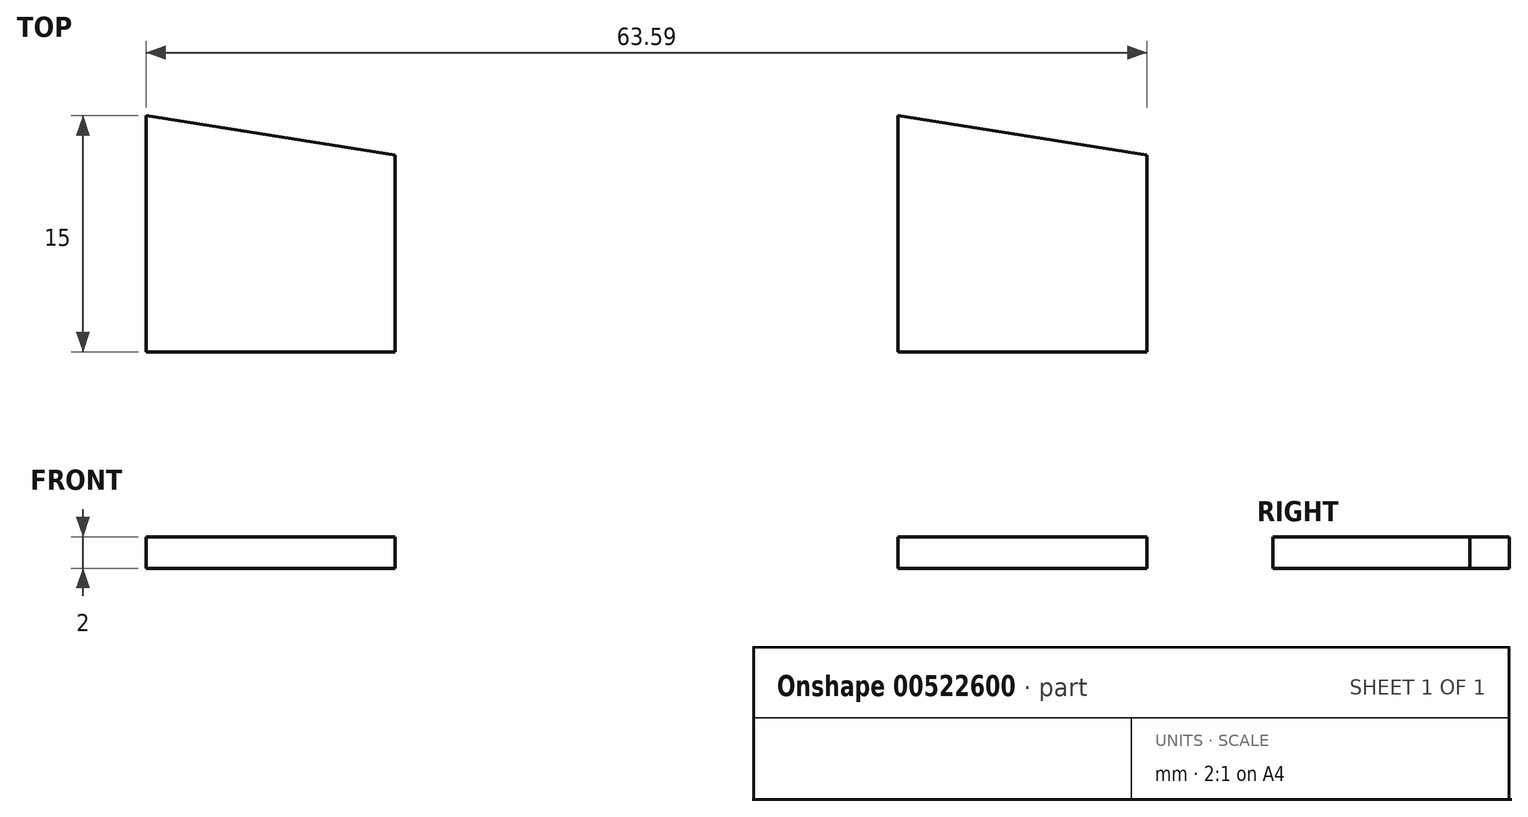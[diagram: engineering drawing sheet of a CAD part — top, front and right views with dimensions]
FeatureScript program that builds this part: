
annotation { "Feature Type Name" : "Feature", "Feature Type Description" : "" }
export const myFeature = defineFeature(function(context is Context, id is Id, definition is map)
    precondition{}
    {
        {
            var Q0;
            Q0=qCreatedBy(makeId("Top.planeOp"),FACE);
            var sketch = newSketch(context, id + "F0", { "sketchPlane" : qUnion([Q0])});
            skLineSegment(sketch, "E0", {"start": v(0, 0) * mm, "end": v(0, 15) * mm});
            skLineSegment(sketch, "E1", {"start": v(0, 0) * mm, "end": v(15.83, 0) * mm});
            skLineSegment(sketch, "E2", {"start": v(15.83, 0) * mm, "end": v(15.83, 12.5) * mm});
            skLineSegment(sketch, "E3", {"start": v(0, 15) * mm, "end": v(15.83, 12.5) * mm});
            skSolve(sketch);
        }
        {
            var Q0;
            Q0 = qSketchRegion(id + "F0", true);
            extrude(context, id + "F1", {"entities" : qUnion([Q0]), "depth" : 2 * mm, "offsetDistance" : 25 * mm});
        }
        {
            var Q0;
            Q0=qCreatedBy(makeId("Top.planeOp"),FACE);
            var sketch = newSketch(context, id + "F2", { "sketchPlane" : qUnion([Q0])});
            skLineSegment(sketch, "E4", {"start": v(-47.76, 0) * mm, "end": v(-47.76, 15) * mm});
            skLineSegment(sketch, "E5", {"start": v(-47.76, 0) * mm, "end": v(-31.93, 0) * mm});
            skLineSegment(sketch, "E6", {"start": v(-31.93, 0) * mm, "end": v(-31.93, 12.5) * mm});
            skLineSegment(sketch, "E7", {"start": v(-47.76, 15) * mm, "end": v(-31.93, 12.5) * mm});
            skSolve(sketch);
        }
        {
            var Q0;
            Q0=makeQuery(id+"F2.imprint","IMPRINT",FACE,{"disambiguationData":[TD([[makeQuery(id+"F2.imprint","IMPRINT",EDGE,{"derivedFrom":sQuery(id+"F2.wireOp",EDGE,"E4")}),-1.0]])]});
            extrude(context, id + "F3", {"entities" : qUnion([Q0]), "depth" : 2 * mm, "offsetDistance" : 25 * mm});
        }
    });
